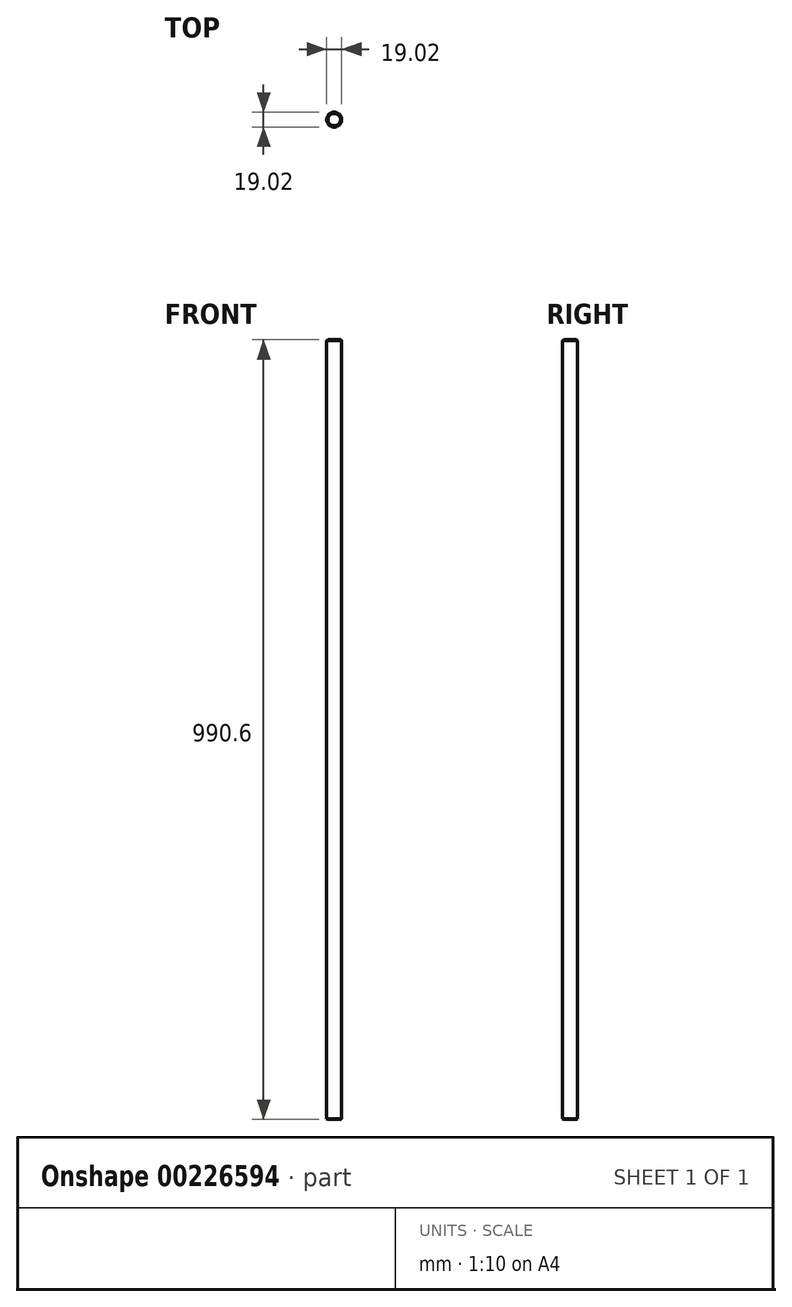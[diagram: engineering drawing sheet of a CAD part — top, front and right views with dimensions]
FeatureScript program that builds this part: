
annotation { "Feature Type Name" : "Feature", "Feature Type Description" : "" }
export const myFeature = defineFeature(function(context is Context, id is Id, definition is map)
    precondition{}
    {
        {
            var Q0;
            Q0=qCreatedBy(makeId("Top.planeOp"),FACE);
            var sketch = newSketch(context, id + "F0", { "sketchPlane" : qUnion([Q0])});
            skCircle(sketch, "E0", {"center": v(0, 0) * mm, "radius": 9.5 * mm});
            skSolve(sketch);
        }
        {
            var Q0;
            Q0=makeQuery(id+"F0.imprint","IMPRINT",FACE,{"disambiguationData":[TD([[makeQuery(id+"F0.imprint","IMPRINT",EDGE,{"derivedFrom":sQuery(id+"F0.wireOp",EDGE,"E0")}),1.0]])]});
            extrude(context, id + "F1", {"entities" : qUnion([Q0]), "oppositeDirection" : true, "offsetDistance" : 25.4 * mm, "depth" : 990.6 * mm});
        }
        {
            var Q0;
            Q0=makeQuery(id+"F1.opExtrude","CAP_EDGE",EDGE,{"disambiguationData":[OSD([sQuery(id+"F0.wireOp",EDGE,"E0")])],"isStart":true});
            var Q1;
            Q1=makeQuery(id+"F1.opExtrude","CAP_EDGE",EDGE,{"disambiguationData":[OSD([sQuery(id+"F0.wireOp",EDGE,"E0")])],"isStart":false});
            chamfer(context, id + "F2", {"entities" : qUnion([Q0, Q1]), "chamferType" : ChamferType.OFFSET_ANGLE, "width" : 1.59 * mm, "oppositeDirection" : false, "angle" : 30 * degree, "tangentPropagation" : true});
        }
    });
